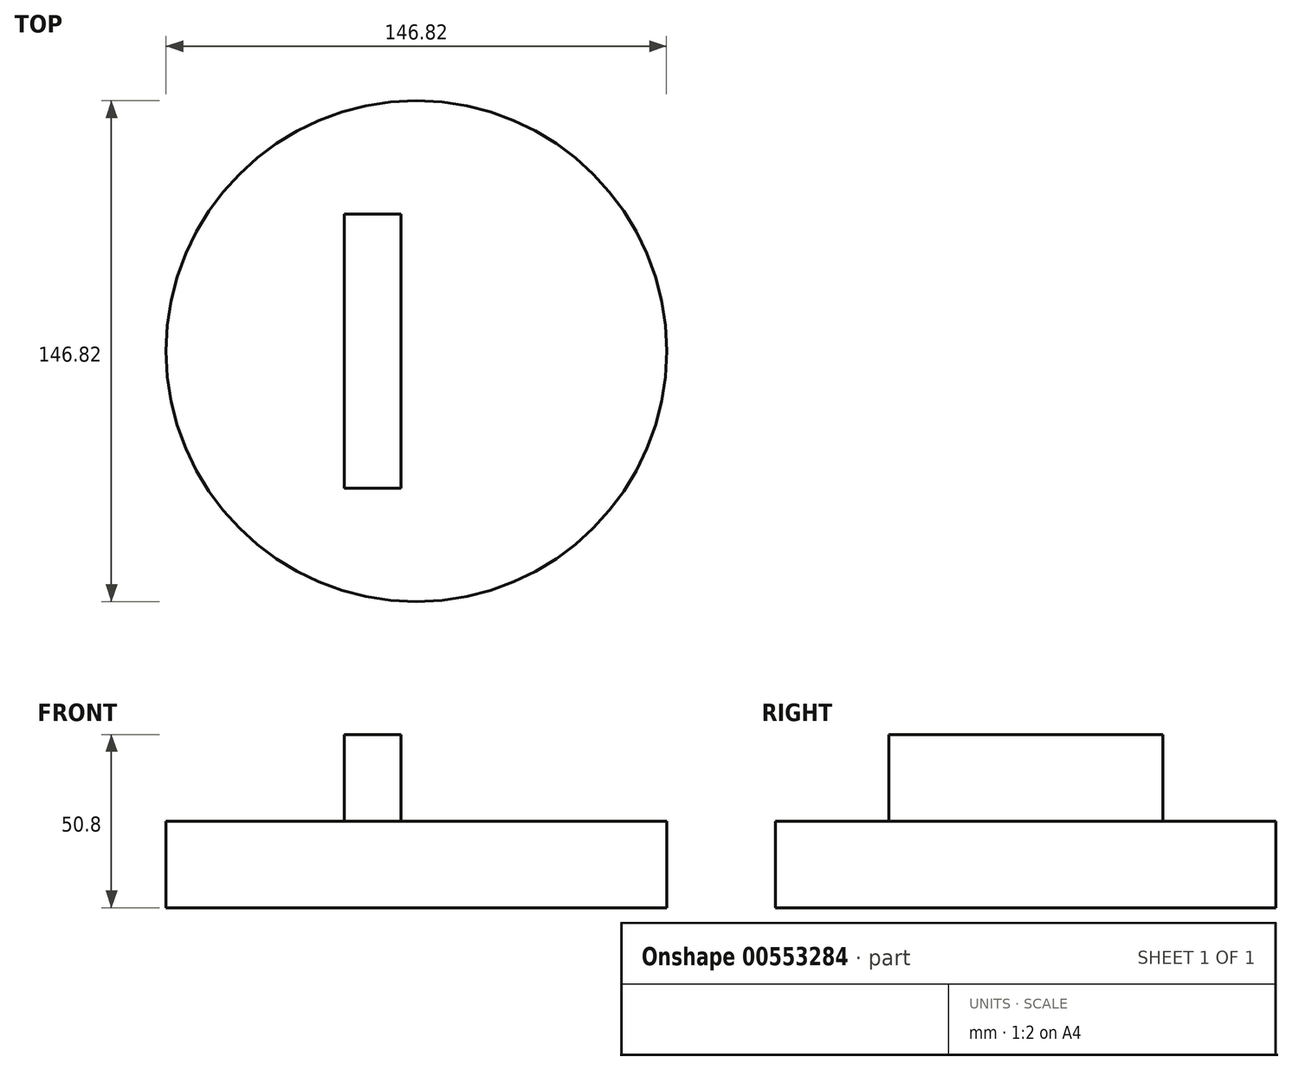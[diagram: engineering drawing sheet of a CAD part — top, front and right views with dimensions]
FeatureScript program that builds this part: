
annotation { "Feature Type Name" : "Feature", "Feature Type Description" : "" }
export const myFeature = defineFeature(function(context is Context, id is Id, definition is map)
    precondition{}
    {
        {
            var Q0;
            Q0=qCreatedBy(makeId("Top.planeOp"),FACE);
            var sketch = newSketch(context, id + "F0", { "sketchPlane" : qUnion([Q0])});
            skCircle(sketch, "E0", {"center": v(0, 0) * mm, "radius": 73.41 * mm});
            skSolve(sketch);
        }
        {
            var Q0;
            Q0 = qSketchRegion(id + "F0", true);
            extrude(context, id + "F1", {"entities" : qUnion([Q0]), "depth" : 25.4 * mm, "offsetDistance" : 25.4 * mm});
        }
        {
            var Q0;
            Q0=makeQuery(id+"F1.opExtrude","CAP_FACE",FACE,{"disambiguationData":[OSD([sQuery(id+"F0.wireOp",EDGE,"E0")])],"isStart":false});
            var sketch = newSketch(context, id + "F2", { "sketchPlane" : qUnion([Q0])});
            skLineSegment(sketch, "E1.bottom", {"start": v(-21.11, 40.19) * mm, "end": v(-4.54, 40.19) * mm});
            skLineSegment(sketch, "E1.top", {"start": v(-21.11, -40.19) * mm, "end": v(-4.54, -40.19) * mm});
            skLineSegment(sketch, "E1.left", {"start": v(-21.11, 40.19) * mm, "end": v(-21.11, -40.19) * mm});
            skLineSegment(sketch, "E1.right", {"start": v(-4.54, 40.19) * mm, "end": v(-4.54, -40.19) * mm});
            skPoint(sketch, "E1.middle", {"position": v(-12.83, 0) * mm});
            skSolve(sketch);
        }
        {
            var Q0;
            Q0 = qSketchRegion(id + "F2", true);
            extrude(context, id + "F3", {"entities" : qUnion([Q0]), "operationType" : NewBodyOperationType.ADD, "depth" : 25.4 * mm, "offsetDistance" : 25.4 * mm});
        }
    });
